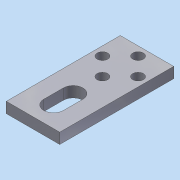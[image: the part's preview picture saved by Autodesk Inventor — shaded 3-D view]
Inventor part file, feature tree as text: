
AUTODESK INVENTOR PART (.ipt)
format: ipt  version: 2013 (Build 170138000, 138)  size: 111,616 bytes
history: native  units: mm
features: sketch x3, extrude x2, hole x1
ambient origin geometry x8: Origin, YZ Plane, XZ Plane, XY Plane, X Axis, Y Axis, Z Axis, Center Point
bodies: Solid1 (feature_tree)
feature tree (6):
  extrude  "Extrusion1"  Depth=15.0mm
  hole  "Hole1"  [1 undecoded]
  extrude  "Extrusion2"  Depth=5.0mm
  sketch  "Sketch1"  dims[d0=32.0mm d2=15.0mm]
  sketch  "Sketch2"  dims[d3=3.0mm d4=0.0mm d5=10.0mm]
  sketch  "Sketch3"  dims[d7=10.0mm d8=5.0mm d9=2.5mm d10=5.0mm d11=3.0mm d12=6.0mm d13=4.0mm d14=2.0mm d15=90.0deg d16=8.0mm d17=20.594885mm d18=5.5mm d20=5.5mm d21=3.02mm d22=3.0mm d23=0.0mm]
note: 1 required parameter value undecoded (feature->parameter linkage not recoverable at this tier; creation-order binding heuristic only, values carry confidence <= 0.55)
